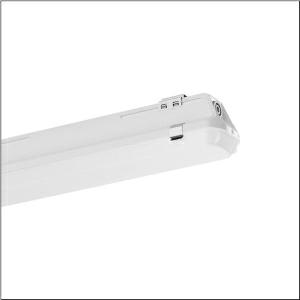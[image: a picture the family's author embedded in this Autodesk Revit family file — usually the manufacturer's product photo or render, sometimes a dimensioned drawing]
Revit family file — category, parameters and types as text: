
# Revit family: monsun_r__11_51fp10dp460h_8c07
name_source: partatom
category: Lighting Fixtures
units: mm (PartAtom-declared; Revit-internal decimal feet)

## family parameters
Cut with Voids When Loaded = No
Host = Face
Light Source = No
Part Type = Normal
Room Calculation Point = No
Round Connector Dimension = Use Diameter
Shared = No

## types (1)
- --- (1 x LED, 6050 lm, 34.6 W, 4000K)
    Apparent Load = 35 VA
    CIE Flux Codes = 47 77 93 94 100
    Color Rendering = 80
    Color Temperature = 4000K
    Default Elevation = 1800 mm
    Description = Monsun® 11, damp-proof luminaire, chain hanger, primary optical cover: enclosure, of PMMA, light emission: direct distribution, primary light characteristic: symmetric, installation type: suspended mounting, surface-mounted, horizontal mounting, vertical mounting, LED, rated luminous flux: 6.050lm, luminous efficacy: 175lm/W, light colour: 840, colour temperature: 4000K, control gear: ECG DALI, with terminal, 5-pole, max. 2.5mm², mains connection: 220..240V, AC, 50/60Hz, rated input power: 35W, luminaire housing, of glass-fibre reinforced polyester, uncoated, bright grey, incl. chain hanger, length: 1.590mm, width: 90mm, height: 88mm, clip for enclosure, of stainless steel (V2A), ceiling mounting element, of stainless steel (V2A), chain hanger, of stainless steel (V2A), protection rating (complete): IP66, insulation class (complete): insulation class I (protective earthing), certification: CE, ENEC, VDE, UKCA, protection symbol: D, impact resistance: IK04, permissible operating ambient temperature: -25..+40°C, standard: EN 50419, EN 60598-2-1, no direct snow, no direct sun, no direct rain, for indoor or canopied outdoor use, corresponds to IFS (International Featured Standards) requirements for safety and quality in the food industry, contact your sales advisor before using the luminaires in applications with unclear chemical exposure, large temperature fluctuations or condensation-forming humidity, LABS conformity tested according to VDMA 24364:2018-05, packaging unit: 1 piece
    Height = 89 mm
    Lamp = 1 x LED
    Lamp Light Flux = 6050 lm
    Lamp Power = 34.6 W
    Lamp count = 1
    Length = 1590 mm
    Luminous efficacy = 175 lm/W
    Manufacturer = Siteco
    ModVariant = No
    Model = 51FP10DP460H
    Mounting Place = Ceiling
    Mounting Type = Surface mounted
    Number of Poles = 1
    OnlyDefault = Yes
    Power Factor = 1
    Product Name = Monsun® 11
    Product group = damp-proof luminaire
    ProductGroupID = 301
    Protection Class = Protection class I
    Protection Degree = IP 66
    RLX_Detail_Level = 1
    RLX_Emergency_Light_Flux = 0 lm
    RLX_Emergency_Type = 0
    RLX_Emergency_Type_DB = No
    RlxData = <blob elided: 92473 chars, md5=ffeb3b4b>
    Socket = socket
    Standby Power = 0 W
    System Light Flux = 6050 lm
    System Power = 35 W
    Type Comments = factory setting: luminous flux: 100 % | dim-lin: 254 | 232 mA
    Type Image = l_1004748.jpg
    URL = http://relux.com
    VarID = @adj_157195
    Voltage = 0 V
    Weight = 0.00 kg
    Width = 90 mm

## geometry (parser evidence)
native form markers: Blend x4, Sweep x11
no freeform markers — native parametric forms only
